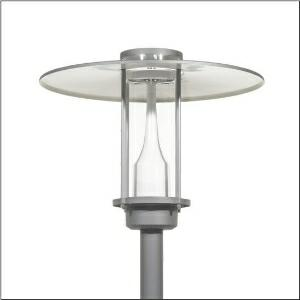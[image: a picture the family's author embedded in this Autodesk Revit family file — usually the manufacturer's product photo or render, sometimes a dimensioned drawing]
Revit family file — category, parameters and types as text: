
# Revit family: city-light_plus_iq___st1_2a_5xa5275mf14h_a6f0
name_source: partatom
category: Lighting Fixtures
units: mm (PartAtom-declared; Revit-internal decimal feet)

## family parameters
Cut with Voids When Loaded = No
Host = Face
Light Source = No
Part Type = Normal
Room Calculation Point = No
Round Connector Dimension = Use Diameter
Shared = No

## types (1)
- --- (1 x LED, 1470 lm, 11.8 W, 2700K)
    Apparent Load = 12 VA
    CIE Flux Codes = 22 62 93 97 100
    Color Rendering = 70
    Color Temperature = 2700K
    Default Elevation = 1800 mm
    Description = City-Light Plus iQ, mast luminaire, Module 540 iQ-SR, primary light control with 3 zone facetted reflector, of plastic, silver coated, highly specular, structured, primary optical cover: cover, of PMMA, transparent, light distribution: ST1.2a, light emission: direct distribution, primary light characteristic: asymmetric, installation type: post-top, LED, High Power LED, rated luminous flux: 1.470lm, luminous efficacy: 125lm/W, light colour: 727, colour temperature: 2700K, control gear: iQ Street-Remote, control: pre-setting: logarithmic dimming characteristic, Street-Remote, Auto-Match, Temp-Guard, Lumen-Switch, Night-Set, Smart-Wire, Light-Fading, Desk-Remote (wireless, voltage-free reading and setting of iQ features in the workshop via application-optimized NFC function/RFID function), optimised constant luminous flux control (CLO 2.0), with terminal, 6-pole, max. 2.5mm², mains connection: 230..240V, AC, 50/60Hz, start of lifetime: 12W, end of service life: 12W, reduction: 6W, luminaire housing, upper part, of glass-fibre reinforced polyester, coated, Siteco® metallic grey (DB 702S), diameter: 750mm, height: 590mm, spigot size: d x l = 76 x 70mm (post-top) | with reducer (optional accessory) 60 x 70mm, mounting height: 3..5m, post-top mast mounting element, of diecast aluminium, coated, Siteco® metallic grey (DB 702S), Module 540 iQ-SR, traffic white (RAL 9016), equipment: standard, protection rating (complete): IP65, insulation class (complete): insulation class II (safety insulation), certification: CE, ENEC, VDE, packaging unit: 1 piece

Light Distribution: ST1.2a
    Height = 590 mm
    Lamp = 1 x LED
    Lamp Light Flux = 1470 lm
    Lamp Power = 11.8 W
    Lamp count = 1
    Length = 750 mm
    Luminous efficacy = 125 lm/W
    Manufacturer = Siteco
    ModVariant = No
    Model = 5XA5275MF14H
    Number of Poles = 1
    OnlyDefault = Yes
    Power Factor = 1
    Product Name = City-Light Plus iQ | ST1.2a
    Product group = mast luminaire | pylon top
    ProductGroupID = 6100
    Protection Class = Protection class II
    Protection Degree = IP 65
    RLX_Detail_Level = 1
    RLX_Emergency_Light_Flux = 0 lm
    RLX_Emergency_Type = 0
    RLX_Emergency_Type_DB = No
    RlxData = <blob elided: 91645 chars, md5=64dc0898>
    Socket = socket
    Standby Power = 0 W
    System Light Flux = 1470 lm
    System Power = 12 W
    Type Comments = factory setting: luminous flux: 100 % | dim-lin: 254 | 472 mA
    Type Image = l_1006456.jpg
    URL = http://relux.com
    VarID = @adj_156974
    Voltage = 0 V
    Weight = 0.00 kg
    Width = 0 mm  [stored 0 ft]

note: [stored X ft] marks values corroborated as IEEE doubles in the binary element streams (Revit-internal decimal feet)

## geometry (parser evidence)
native form markers: Blend x4, Sweep x11
no freeform markers — native parametric forms only
